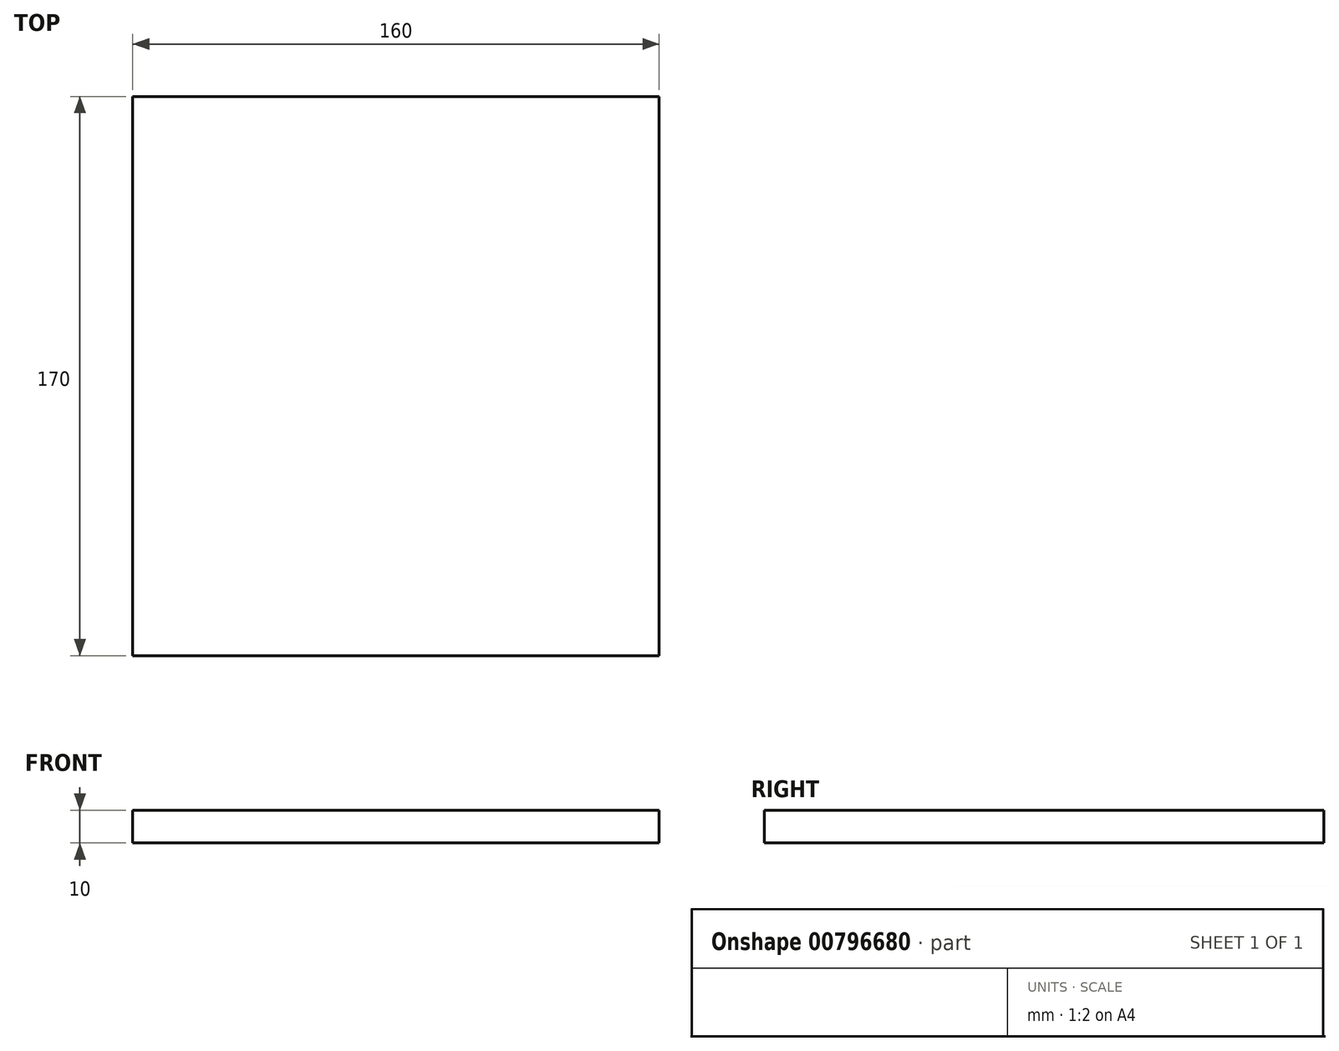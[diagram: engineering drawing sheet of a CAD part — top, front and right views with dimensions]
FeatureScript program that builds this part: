
annotation { "Feature Type Name" : "Feature", "Feature Type Description" : "" }
export const myFeature = defineFeature(function(context is Context, id is Id, definition is map)
    precondition{}
    {
        {
            var Q0;
            Q0=qCreatedBy(makeId("Front.planeOp"),FACE);
            var sketch = newSketch(context, id + "F0", { "sketchPlane" : qUnion([Q0])});
            skLineSegment(sketch, "E0.bottom", {"start": v(80, 5) * mm, "end": v(-80, 5) * mm});
            skLineSegment(sketch, "E0.top", {"start": v(80, -5) * mm, "end": v(-80, -5) * mm});
            skLineSegment(sketch, "E0.left", {"start": v(80, 5) * mm, "end": v(80, -5) * mm});
            skLineSegment(sketch, "E0.right", {"start": v(-80, 5) * mm, "end": v(-80, -5) * mm});
            skPoint(sketch, "E0.middle", {"position": v(0, 0) * mm});
            skSolve(sketch);
        }
        {
            var Q0;
            Q0=makeQuery(id+"F0.imprint","IMPRINT",FACE,{"disambiguationData":[TD([[makeQuery(id+"F0.imprint","IMPRINT",EDGE,{"derivedFrom":sQuery(id+"F0.wireOp",EDGE,"E0.bottom")}),1.0]])]});
            extrude(context, id + "F1", {"entities" : qUnion([Q0]), "depth" : 170 * mm, "offsetDistance" : 25 * mm});
        }
    });
